# Revit family: Gas-Detector-Controller-DVP-1200-Aerionics
name_source: partatom
category: Mechanical Equipment
units: mm (PartAtom-declared; Revit-internal decimal feet)

## family parameters
Always vertical = Yes
Classification Number = 23.65.00.00
Cut with Voids When Loaded = No
Host = Wall
Maintain Annotation Orientation = No
Part Type = Normal
Room Calculation Point = No
Round Connector Dimension = Use Diameter
Shared = No

## types (1)
- DVP-1200
    Categories = Control Panels, HVAC/R, Electrical
    Comments = The DVP-1200 controller in conjunction with Macurco gas detectors provides automatic control to help maintain an acceptable environment in parking garages or other applications. This control panel offers an expandable system with up to 192 addressable detectors in the field. The DVP-1200 comes standard with four relays, as well as expandable onboard relay options (+2, +4). Other outputs on the DVP-1200 include three analog outputs, four 24VDC drivers, and BACnet IP. The DVP-1200 can be connected to up to two remote relay boxes with each remote relay box containing two relays. With the expandability of this panel, the DVP-1200 will fit into any gas detection application.- ETL Listed
    Default Elevation = 0 "
    Manufacturer = MACURCO
    Model Name = DVP-1200-Digital w/ BACnet IP
    Tags = Arenas, Commercial Applications, Loading Docks, Parking Garages, Warehouses
    Type Comments = Do not paint
    URL = https://www.macurco.com

## geometry (parser evidence)
native form markers: Sweep x3
no freeform markers — native parametric forms only
